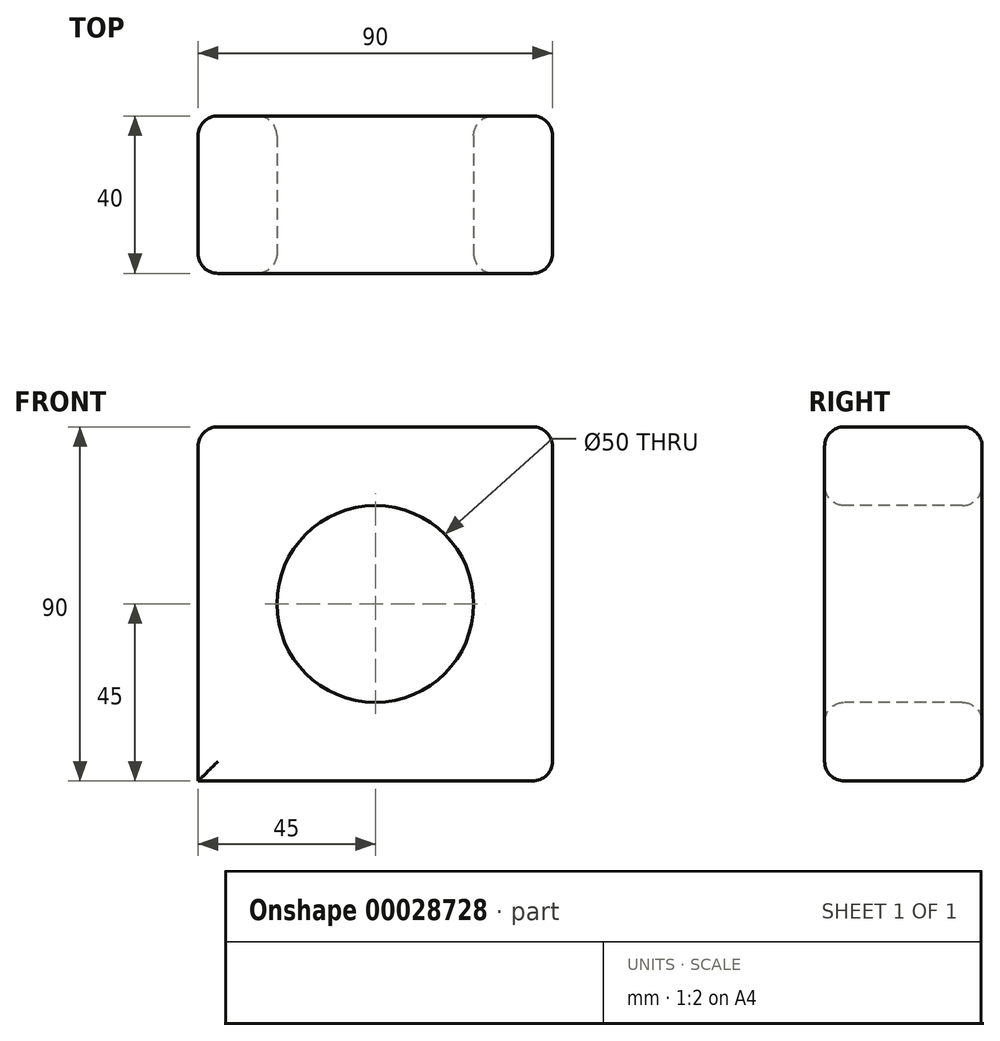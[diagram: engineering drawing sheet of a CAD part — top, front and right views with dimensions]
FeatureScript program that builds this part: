
annotation { "Feature Type Name" : "Feature", "Feature Type Description" : "" }
export const myFeature = defineFeature(function(context is Context, id is Id, definition is map)
    precondition{}
    {
        {
            var Q0;
            Q0=qCreatedBy(makeId("Front.planeOp"),FACE);
            var sketch = newSketch(context, id + "F0", { "sketchPlane" : qUnion([Q0])});
            skCircle(sketch, "E0", {"center": v(0, 0) * mm, "radius": 25 * mm});
            skLineSegment(sketch, "E1.rect.bottom", {"start": v(-45, 45) * mm, "end": v(45, 45) * mm});
            skLineSegment(sketch, "E1.rect.top", {"start": v(-45, -45) * mm, "end": v(45, -45) * mm});
            skLineSegment(sketch, "E1.rect.left", {"start": v(-45, 45) * mm, "end": v(-45, -45) * mm});
            skLineSegment(sketch, "E1.rect.right", {"start": v(45, 45) * mm, "end": v(45, -45) * mm});
            skSolve(sketch);
        }
        {
            var Q0;
            Q0=makeQuery(id+"F0.imprint","IMPRINT",FACE,{"disambiguationData":[TD([[makeQuery(id+"F0.imprint","IMPRINT",EDGE,{"derivedFrom":sQuery(id+"F0.wireOp",EDGE,"E0")}),-1.0]])]});
            extrude(context, id + "F1", {"entities" : qUnion([Q0]), "oppositeDirection" : true, "depth" : 40 * mm});
        }
        {
            var Q0;
            Q0=makeQuery(id+"F1.opExtrude","CAP_EDGE",EDGE,{"disambiguationData":[OSD([sQuery(id+"F0.wireOp",EDGE,"E1.rect.right")])],"isStart":false});
            var Q1;
            Q1=makeQuery(id+"F1.opExtrude","CAP_EDGE",EDGE,{"disambiguationData":[OSD([sQuery(id+"F0.wireOp",EDGE,"E1.rect.bottom")])],"isStart":false});
            var Q2;
            Q2=makeQuery(id+"F1.opExtrude","CAP_EDGE",EDGE,{"disambiguationData":[OSD([sQuery(id+"F0.wireOp",EDGE,"E1.rect.left")])],"isStart":false});
            var Q3;
            Q3=makeQuery(id+"F1.opExtrude","CAP_FACE",FACE,{"disambiguationData":[OSD([sQuery(id+"F0.wireOp",EDGE,"E0"),sQuery(id+"F0.wireOp",EDGE,"E1.rect.bottom"),sQuery(id+"F0.wireOp",EDGE,"E1.rect.top"),sQuery(id+"F0.wireOp",EDGE,"E1.rect.left"),sQuery(id+"F0.wireOp",EDGE,"E1.rect.right")])],"isStart":false});
            var Q4;
            Q4=makeQuery(id+"F1.opExtrude","SWEPT_FACE",FACE,{"disambiguationData":[OSD([sQuery(id+"F0.wireOp",EDGE,"E1.rect.bottom")])]});
            var Q5;
            Q5=makeQuery(id+"F1.opExtrude","CAP_EDGE",EDGE,{"disambiguationData":[OSD([sQuery(id+"F0.wireOp",EDGE,"E1.rect.left")])],"isStart":true});
            var Q6;
            Q6=makeQuery(id+"F1.opExtrude","SWEPT_FACE",FACE,{"disambiguationData":[OSD([sQuery(id+"F0.wireOp",EDGE,"E1.rect.right")])]});
            var Q7;
            Q7=makeQuery(id+"F1.opExtrude","CAP_EDGE",EDGE,{"disambiguationData":[OSD([sQuery(id+"F0.wireOp",EDGE,"E1.rect.top")])],"isStart":true});
            var Q8;
            Q8=makeQuery(id+"F1.opExtrude","CAP_EDGE",EDGE,{"disambiguationData":[OSD([sQuery(id+"F0.wireOp",EDGE,"E0")])],"isStart":true});
            fillet(context, id + "F2", {"entities" : qUnion([Q0, Q1, Q2, Q3, Q4, Q5, Q6, Q7, Q8]), "radius" : 5 * mm, "tangentPropagation" : true, "allowEdgeOverflow" : false});
        }
    });
